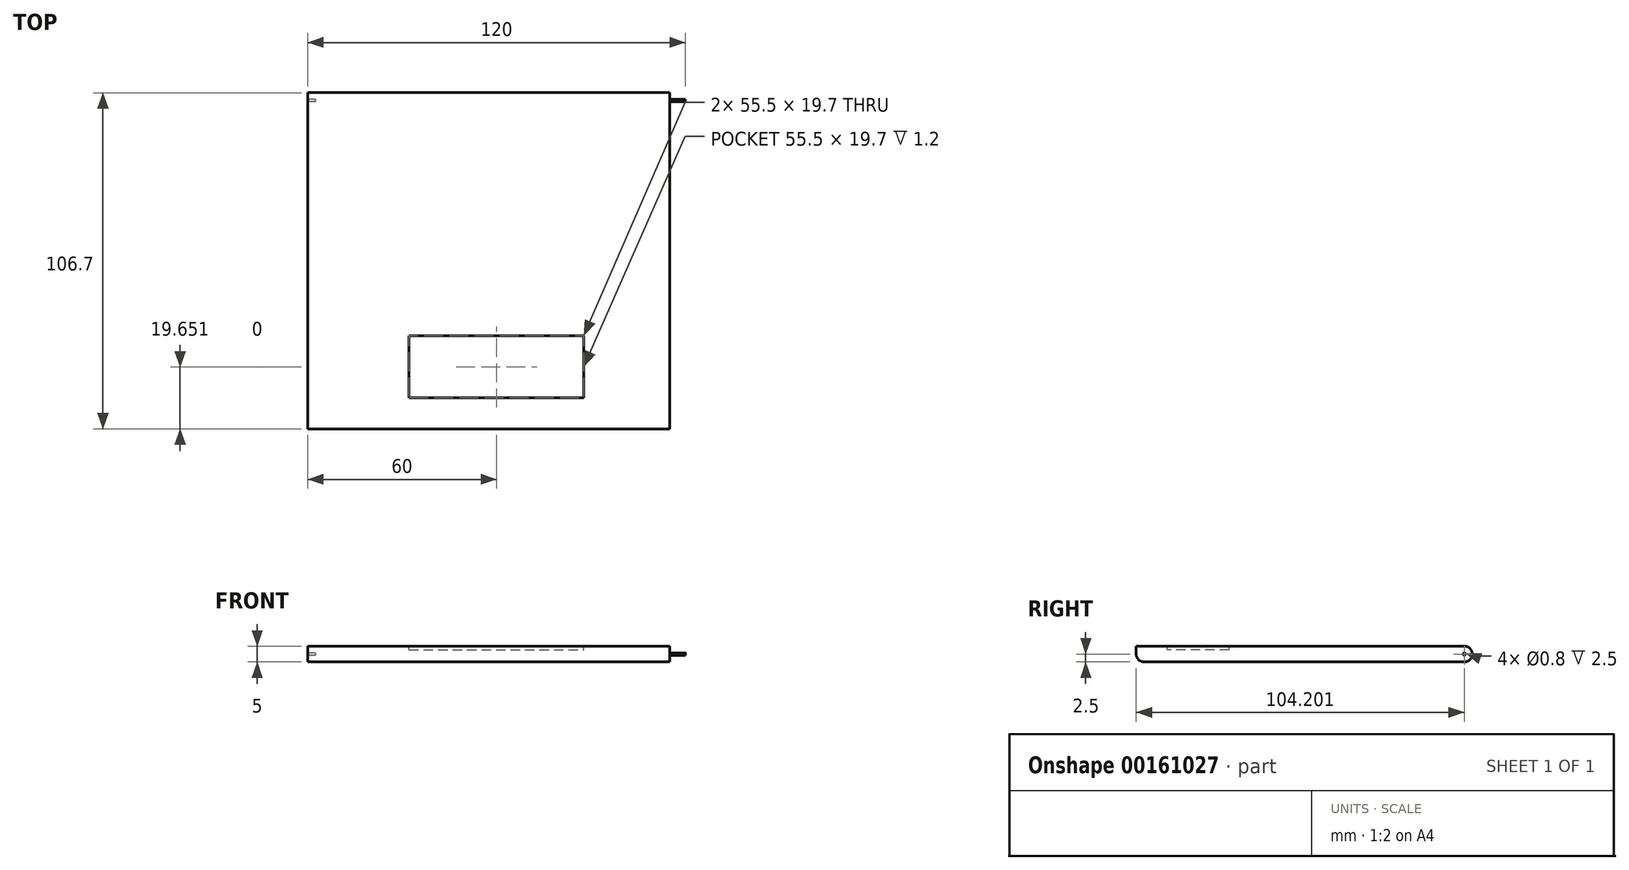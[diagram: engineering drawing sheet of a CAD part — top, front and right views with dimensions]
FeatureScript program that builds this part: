
annotation { "Feature Type Name" : "Feature", "Feature Type Description" : "" }
export const myFeature = defineFeature(function(context is Context, id is Id, definition is map)
    precondition{}
    {
        {
            var Q0;
            Q0=qCreatedBy(makeId("Top.planeOp"),FACE);
            var sketch = newSketch(context, id + "F0", { "sketchPlane" : qUnion([Q0])});
            skLineSegment(sketch, "E0", {"start": v(0, 45.71) * mm, "end": v(0, -6.69) * mm, "construction": true});
            skLineSegment(sketch, "E1.bottom", {"start": v(0, 45.71) * mm, "end": v(-45.2, 45.71) * mm});
            skLineSegment(sketch, "E1.top", {"start": v(0, -6.69) * mm, "end": v(-45.2, -6.69) * mm});
            skLineSegment(sketch, "E1.right", {"start": v(-45.2, 45.71) * mm, "end": v(-45.2, -6.69) * mm});
            skLineSegment(sketch, "E2.bottom", {"start": v(0, -16.69) * mm, "end": v(-27.75, -16.69) * mm});
            skLineSegment(sketch, "E2.top", {"start": v(-0.7, -36.39) * mm, "end": v(-27.75, -36.39) * mm});
            skLineSegment(sketch, "E2.right", {"start": v(-27.75, -16.69) * mm, "end": v(-27.75, -36.39) * mm});
            skLineSegment(sketch, "E3.bottom", {"start": v(0, 60.71) * mm, "end": v(-60.2, 60.71) * mm});
            skLineSegment(sketch, "E3.top", {"start": v(-0.7, -46.39) * mm, "end": v(-60.2, -46.39) * mm});
            skLineSegment(sketch, "E3.right", {"start": v(-60.2, 60.71) * mm, "end": v(-60.2, -46.39) * mm});
            skLineSegment(sketch, "E4.MirrorCS", {"start": v(-0.7, -46.39) * mm, "end": v(60.2, -46.39) * mm});
            skLineSegment(sketch, "E5.MirrorCS", {"start": v(-0.7, -36.39) * mm, "end": v(27.75, -36.39) * mm});
            skLineSegment(sketch, "E6.MirrorCS", {"start": v(27.75, -16.69) * mm, "end": v(27.75, -36.39) * mm});
            skLineSegment(sketch, "E7.MirrorCS", {"start": v(0, -16.69) * mm, "end": v(27.75, -16.69) * mm});
            skLineSegment(sketch, "E8.MirrorCS", {"start": v(0, -6.69) * mm, "end": v(45.2, -6.69) * mm});
            skLineSegment(sketch, "E9.MirrorCS", {"start": v(60.2, 60.71) * mm, "end": v(60.2, -46.39) * mm});
            skLineSegment(sketch, "E10.MirrorCS", {"start": v(45.2, 45.71) * mm, "end": v(45.2, -6.69) * mm});
            skLineSegment(sketch, "E11.MirrorCS", {"start": v(0, 60.71) * mm, "end": v(60.2, 60.71) * mm});
            skLineSegment(sketch, "E12.MirrorCS", {"start": v(0, 45.71) * mm, "end": v(45.2, 45.71) * mm});
            skLineSegment(sketch, "E13", {"start": v(-60.2, 60.71) * mm, "end": v(-63.2, 60.71) * mm});
            skLineSegment(sketch, "E14", {"start": v(-63.2, 60.71) * mm, "end": v(-63.2, -46.39) * mm});
            skLineSegment(sketch, "E15", {"start": v(-63.2, -46.39) * mm, "end": v(-60.2, -46.39) * mm});
            skLineSegment(sketch, "E16.MirrorCS", {"start": v(63.2, -46.39) * mm, "end": v(60.2, -46.39) * mm});
            skLineSegment(sketch, "E17.MirrorCS", {"start": v(63.2, 60.71) * mm, "end": v(63.2, -46.39) * mm});
            skLineSegment(sketch, "E18.MirrorCS", {"start": v(60.2, 60.71) * mm, "end": v(63.2, 60.71) * mm});
            skPoint(sketch, "E19.orphan", {"position": v(0.7, -36.39) * mm});
            skPoint(sketch, "E20.orphan", {"position": v(0.7, -46.39) * mm});
            skSolve(sketch);
        }
        {
            var Q0;
            Q0=qCreatedBy(makeId("Top.planeOp"),FACE);
            var sketch = newSketch(context, id + "F1", { "sketchPlane" : qUnion([Q0])});
            skLineSegment(sketch, "E21.0", {"start": v(-60.2, 60.71) * mm, "end": v(-60.2, -46.39) * mm, "construction": true});
            skLineSegment(sketch, "E21.1", {"start": v(0, 60.71) * mm, "end": v(-60.2, 60.71) * mm, "construction": true});
            skLineSegment(sketch, "E21.2", {"start": v(0, 60.71) * mm, "end": v(60.2, 60.71) * mm, "construction": true});
            skLineSegment(sketch, "E21.3", {"start": v(60.2, 60.71) * mm, "end": v(60.2, -46.39) * mm, "construction": true});
            skLineSegment(sketch, "E21.4", {"start": v(-0.7, -46.39) * mm, "end": v(60.2, -46.39) * mm, "construction": true});
            skLineSegment(sketch, "E21.5", {"start": v(-0.7, -46.39) * mm, "end": v(-60.2, -46.39) * mm, "construction": true});
            skLineSegment(sketch, "E22.0", {"start": v(0, -16.69) * mm, "end": v(-27.75, -16.69) * mm});
            skLineSegment(sketch, "E22.1", {"start": v(-27.75, -16.69) * mm, "end": v(-27.75, -36.39) * mm});
            skLineSegment(sketch, "E22.2", {"start": v(-0.7, -36.39) * mm, "end": v(-27.75, -36.39) * mm});
            skLineSegment(sketch, "E22.3", {"start": v(-0.7, -36.39) * mm, "end": v(27.75, -36.39) * mm});
            skLineSegment(sketch, "E22.4", {"start": v(27.75, -16.69) * mm, "end": v(27.75, -36.39) * mm});
            skLineSegment(sketch, "E22.5", {"start": v(0, -16.69) * mm, "end": v(27.75, -16.69) * mm});
            skLineSegment(sketch, "E23.0", {"start": v(-0.7, -46.19) * mm, "end": v(60, -46.19) * mm});
            skLineSegment(sketch, "E23.1", {"start": v(-60, 60.51) * mm, "end": v(-60, -46.19) * mm});
            skLineSegment(sketch, "E23.2", {"start": v(0, 60.51) * mm, "end": v(-60, 60.51) * mm});
            skLineSegment(sketch, "E23.3", {"start": v(-0.7, -46.19) * mm, "end": v(-60, -46.19) * mm});
            skLineSegment(sketch, "E23.4", {"start": v(0, 60.51) * mm, "end": v(60, 60.51) * mm});
            skLineSegment(sketch, "E23.5", {"start": v(60, 60.51) * mm, "end": v(60, -46.19) * mm});
            skSolve(sketch);
        }
        {
            var Q0;
            Q0 = qSketchRegion(id + "F1", true);
            var Q1;
            Q1=makeQuery(id+"F1.imprint","IMPRINT",FACE,{"disambiguationData":[TD([[makeQuery(id+"F1.imprint","IMPRINT",EDGE,{"derivedFrom":sQuery(id+"F1.wireOp",EDGE,"E22.0")}),1.0]])]});
            extrude(context, id + "F2", {"entities" : qUnion([Q0, Q1]), "oppositeDirection" : true, "depth" : 5 * mm});
        }
        {
            var Q0;
            Q0=makeQuery(id+"F1.imprint","IMPRINT",FACE,{"disambiguationData":[TD([[makeQuery(id+"F1.imprint","IMPRINT",EDGE,{"derivedFrom":sQuery(id+"F1.wireOp",EDGE,"E22.0")}),1.0]])]});
            extrude(context, id + "F3", {"entities" : qUnion([Q0]), "operationType" : NewBodyOperationType.REMOVE, "oppositeDirection" : true, "depth" : 1.2 * mm});
        }
        {
            var Q0;
            Q0=makeQuery(id+"F2.opExtrude","SWEPT_FACE",FACE,{"disambiguationData":[OSD([sQuery(id+"F1.wireOp",EDGE,"E23.1")])]});
            var sketch = newSketch(context, id + "F4", { "sketchPlane" : qUnion([Q0])});
            skLineSegment(sketch, "E24.0", {"start": v(-60.51, -5) * mm, "end": v(-60.51, 0) * mm, "construction": true});
            skLineSegment(sketch, "E25", {"start": v(-60.51, -5) * mm, "end": v(-55.51, -5) * mm, "construction": true});
            skLineSegment(sketch, "E26", {"start": v(-55.51, -5) * mm, "end": v(-55.51, 0) * mm, "construction": true});
            skLineSegment(sketch, "E27", {"start": v(-55.51, 0) * mm, "end": v(-60.51, 0) * mm, "construction": true});
            skCircle(sketch, "E28", {"center": v(-58.01, -2.5) * mm, "radius": 0.4 * mm});
            skPoint(sketch, "E28.centerSnap0", {"position": v(-60.51, -2.5) * mm});
            skPoint(sketch, "E28.centerSnap1", {"position": v(-58.01, -5) * mm});
            skSolve(sketch);
        }
        {
            var Q0;
            Q0=makeQuery(id+"F4.imprint","IMPRINT",FACE,{"disambiguationData":[TD([[makeQuery(id+"F4.imprint","IMPRINT",EDGE,{"derivedFrom":sQuery(id+"F4.wireOp",EDGE,"E28")}),1.0]])]});
            extrude(context, id + "F5", {"entities" : qUnion([Q0]), "operationType" : NewBodyOperationType.REMOVE, "endBound" : BoundingType.SYMMETRIC, "oppositeDirection" : true, "depth" : 5 * mm});
        }
        {
            var Q0;
            Q0=makeQuery(id+"F2.opExtrude","SWEPT_FACE",FACE,{"disambiguationData":[OSD([sQuery(id+"F1.wireOp",EDGE,"E23.5")])]});
            var sketch = newSketch(context, id + "F6", { "sketchPlane" : qUnion([Q0])});
            skCircle(sketch, "E29.0", {"center": v(58.01, -2.5) * mm, "radius": 0.4 * mm});
            skSolve(sketch);
        }
        {
            var Q0;
            Q0=makeQuery(id+"F6.imprint","IMPRINT",FACE,{"disambiguationData":[TD([[makeQuery(id+"F6.imprint","IMPRINT",EDGE,{"derivedFrom":sQuery(id+"F6.wireOp",EDGE,"E29.0")}),-1.0]])]});
            var Q1;
            Q1=sQuery(id+"F6.wireOp",EDGE,"E29.0");
            extrude(context, id + "F7", {"entities" : qUnion([Q0]), "operationType" : NewBodyOperationType.REMOVE, "surfaceEntities" : qUnion([Q1]), "oppositeDirection" : true, "depth" : 5 * mm});
        }
        {
            var Q0;
            Q0=makeQuery(id+"F2.opExtrude","CAP_EDGE",EDGE,{"disambiguationData":[OSD([sQuery(id+"F1.wireOp",EDGE,"E23.2"),sQuery(id+"F1.wireOp",EDGE,"E23.4")])],"isStart":true});
            var Q1;
            Q1=makeQuery(id+"F2.opExtrude","CAP_EDGE",EDGE,{"disambiguationData":[OSD([sQuery(id+"F1.wireOp",EDGE,"E23.2"),sQuery(id+"F1.wireOp",EDGE,"E23.4")])],"isStart":false});
            fillet(context, id + "F8", {"entities" : qUnion([Q0, Q1]), "radius" : 2.5 * mm, "tangentPropagation" : true, "allowEdgeOverflow" : false});
        }
        {
            var Q0;
            Q0=makeQuery(id+"F2.opExtrude","CAP_EDGE",EDGE,{"disambiguationData":[OSD([sQuery(id+"F1.wireOp",EDGE,"E23.0"),sQuery(id+"F1.wireOp",EDGE,"E23.3")])],"isStart":false});
            fillet(context, id + "F9", {"entities" : qUnion([Q0]), "radius" : 2.5 * mm, "tangentPropagation" : true, "allowEdgeOverflow" : false});
        }
    });
